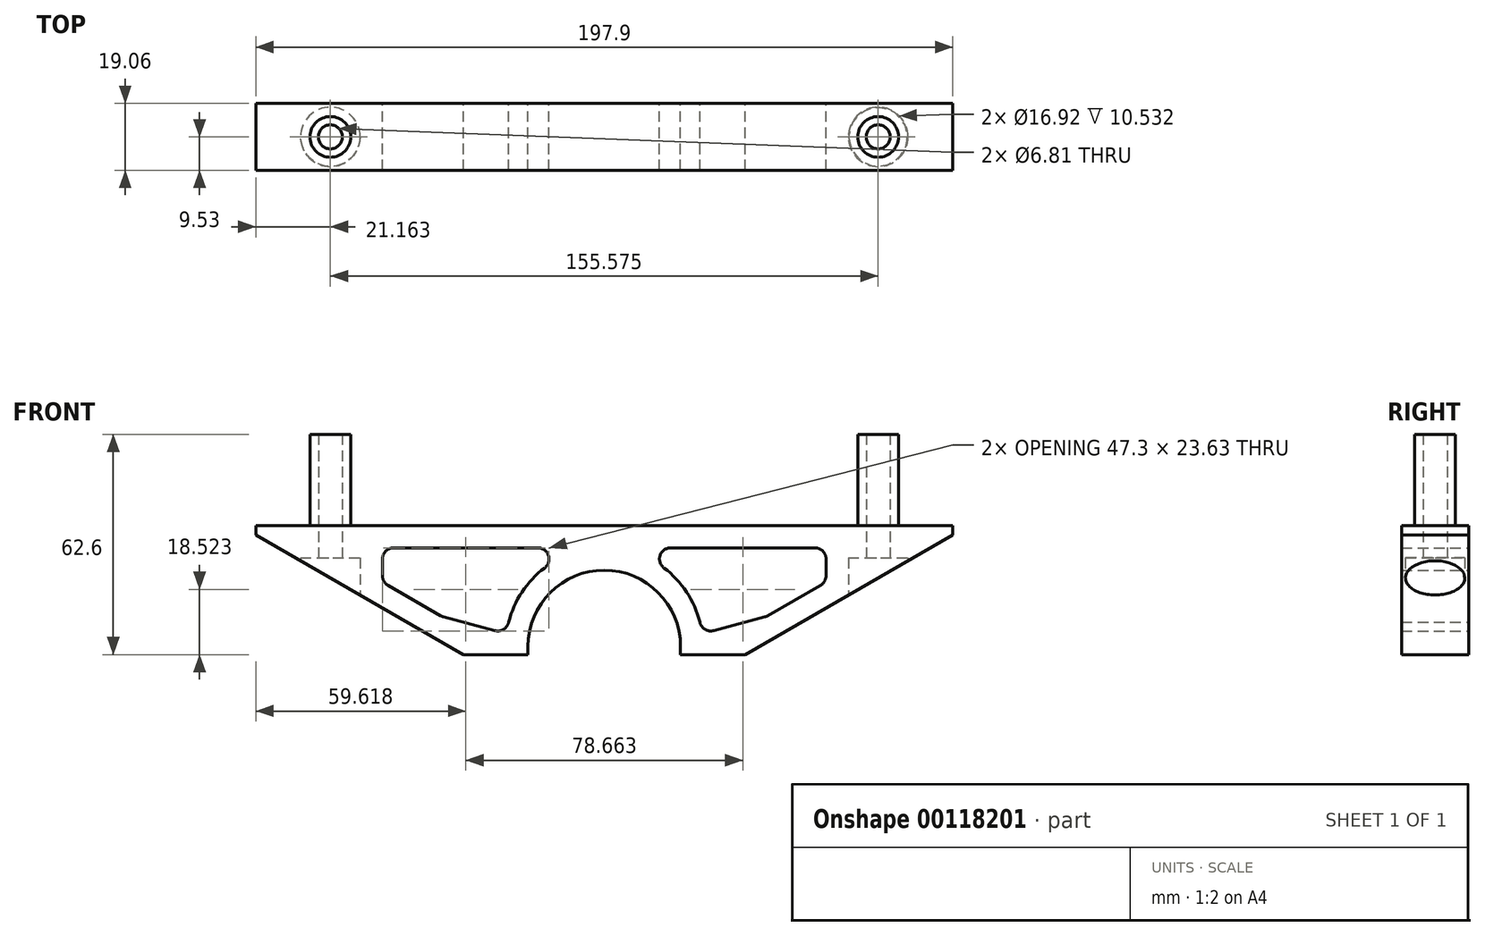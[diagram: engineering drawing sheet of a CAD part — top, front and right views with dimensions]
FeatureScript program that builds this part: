
annotation { "Feature Type Name" : "Feature", "Feature Type Description" : "" }
export const myFeature = defineFeature(function(context is Context, id is Id, definition is map)
    precondition{}
    {
        {
            var Q0;
            Q0=qCreatedBy(makeId("Front.planeOp"),FACE);
            var sketch = newSketch(context, id + "F0", { "sketchPlane" : qUnion([Q0])});
            skLineSegment(sketch, "E0", {"start": v(0, 0) * mm, "end": v(0, 74.83) * mm, "construction": true});
            skLineSegment(sketch, "E1", {"start": v(40, 0) * mm, "end": v(21.65, 0) * mm});
            skArc(sketch, "E2", {"start": v(21.65, 2.33) * mm, "mid": v(0, 23.99) * mm, "end": v(-21.65, 2.33) * mm});
            skArc(sketch, "E3", {"start": v(27.19, 9.05) * mm, "mid": v(23.4, 17.72) * mm, "end": v(16.94, 24.63) * mm});
            skLineSegment(sketch, "E4", {"start": v(-98.95, 36.69) * mm, "end": v(98.95, 36.69) * mm});
            skLineSegment(sketch, "E5", {"start": v(40, 0) * mm, "end": v(98.95, 34.03) * mm});
            skLineSegment(sketch, "E6", {"start": v(-40, 0) * mm, "end": v(-98.95, 34.03) * mm});
            skLineSegment(sketch, "E7", {"start": v(-98.95, 36.69) * mm, "end": v(-98.95, 34.03) * mm});
            skLineSegment(sketch, "E8", {"start": v(98.95, 36.69) * mm, "end": v(98.95, 34.03) * mm});
            skLineSegment(sketch, "E9", {"start": v(21.65, 2.33) * mm, "end": v(21.65, -7.41) * mm});
            skLineSegment(sketch, "E10", {"start": v(-21.65, 2.33) * mm, "end": v(-21.65, 0) * mm});
            skLineSegment(sketch, "E11.trimOffspring", {"start": v(-21.65, 0) * mm, "end": v(-40, 0) * mm});
            skArc(sketch, "E12", {"start": v(18.86, 30.34) * mm, "mid": v(15.85, 28.18) * mm, "end": v(16.94, 24.63) * mm});
            skArc(sketch, "E13", {"start": v(27.16, 9.17) * mm, "mid": v(28.61, 7.16) * mm, "end": v(31.07, 6.81) * mm});
            skArc(sketch, "E14", {"start": v(45.65, 10.72) * mm, "mid": v(46.04, 10.85) * mm, "end": v(46.42, 11.03) * mm});
            skLineSegment(sketch, "E15", {"start": v(18.86, 30.34) * mm, "end": v(59.8, 30.34) * mm});
            skLineSegment(sketch, "E16", {"start": v(62.98, 27.16) * mm, "end": v(62.98, 22.43) * mm});
            skLineSegment(sketch, "E17", {"start": v(61.4, 19.68) * mm, "end": v(46.42, 11.03) * mm});
            skLineSegment(sketch, "E18", {"start": v(45.65, 10.72) * mm, "end": v(31.07, 6.81) * mm});
            skArc(sketch, "E19.trimOffspring", {"start": v(62.98, 27.16) * mm, "mid": v(62.05, 29.4) * mm, "end": v(59.8, 30.34) * mm});
            skArc(sketch, "E20.trimOffspring", {"start": v(61.4, 19.68) * mm, "mid": v(62.55, 20.84) * mm, "end": v(62.98, 22.43) * mm});
            skArc(sketch, "E21.MirrorCS", {"start": v(-18.86, 30.34) * mm, "mid": v(-15.85, 28.18) * mm, "end": v(-16.94, 24.63) * mm});
            skLineSegment(sketch, "E22.MirrorCS", {"start": v(-18.86, 30.34) * mm, "end": v(-59.8, 30.34) * mm});
            skArc(sketch, "E23.MirrorCS", {"start": v(-27.19, 9.05) * mm, "mid": v(-23.4, 17.72) * mm, "end": v(-16.94, 24.63) * mm});
            skArc(sketch, "E24.MirrorCS", {"start": v(-27.16, 9.17) * mm, "mid": v(-28.61, 7.16) * mm, "end": v(-31.07, 6.81) * mm});
            skArc(sketch, "E25.MirrorCS", {"start": v(-45.65, 10.72) * mm, "mid": v(-46.04, 10.85) * mm, "end": v(-46.42, 11.03) * mm});
            skLineSegment(sketch, "E26.MirrorCS", {"start": v(-61.4, 19.68) * mm, "end": v(-46.42, 11.03) * mm});
            skLineSegment(sketch, "E27.MirrorCS", {"start": v(-62.98, 27.16) * mm, "end": v(-62.98, 22.43) * mm});
            skArc(sketch, "E28.MirrorCS", {"start": v(-62.98, 27.16) * mm, "mid": v(-62.05, 29.4) * mm, "end": v(-59.8, 30.34) * mm});
            skLineSegment(sketch, "E29.MirrorCS", {"start": v(-45.65, 10.72) * mm, "end": v(-31.07, 6.81) * mm});
            skArc(sketch, "E30.MirrorCS", {"start": v(-61.4, 19.68) * mm, "mid": v(-62.55, 20.84) * mm, "end": v(-62.98, 22.43) * mm});
            skSolve(sketch);
        }
        {
            var Q0;
            {var subQ8=sQuery(id+"F0.wireOp",EDGE,"E1");Q0=makeQuery(id+"F0.imprint","IMPRINT",FACE,{"disambiguationData":[TD([[makeQuery(id+"F0.imprint","IMPRINT",EDGE,{"derivedFrom":subQ8}),-1.0]])]});}
            extrude(context, id + "F1", {"entities" : qUnion([Q0]), "endBound" : BoundingType.SYMMETRIC, "depth" : 19.05 * mm});
        }
        {
            var Q0;
            Q0=makeQuery(id+"F1.opExtrude","SWEPT_FACE",FACE,{"disambiguationData":[OSD([sQuery(id+"F0.wireOp",EDGE,"E11.trimOffspring")])]});
            cPlane(context, id + "F2", {"entities" : qUnion([Q0]), "cplaneType" : CPlaneType.OFFSET, "offset" : 0 * mm, "width" : 152.4 * mm, "height" : 152.4 * mm});
        }
        {
            var Q0;
            Q0=qCreatedBy(id+"F2.planeOp",FACE);
            var sketch = newSketch(context, id + "F3", { "sketchPlane" : qUnion([Q0])});
            skCircle(sketch, "E31", {"center": v(-77.79, 0) * mm, "radius": 8.46 * mm});
            skCircle(sketch, "E32", {"center": v(77.79, 0) * mm, "radius": 8.46 * mm});
            skSolve(sketch);
        }
        {
            var Q0;
            Q0=makeQuery(id+"F3.imprint","IMPRINT",FACE,{"disambiguationData":[TD([[makeQuery(id+"F3.imprint","IMPRINT",EDGE,{"derivedFrom":sQuery(id+"F3.wireOp",EDGE,"E31")}),1.0]])]});
            var Q1;
            Q1=makeQuery(id+"F3.imprint","IMPRINT",FACE,{"disambiguationData":[TD([[makeQuery(id+"F3.imprint","IMPRINT",EDGE,{"derivedFrom":sQuery(id+"F3.wireOp",EDGE,"E32")}),1.0]])]});
            extrude(context, id + "F4", {"entities" : qUnion([Q0, Q1]), "operationType" : NewBodyOperationType.REMOVE, "oppositeDirection" : true, "depth" : 27.46 * mm});
        }
        {
            var Q0;
            Q0=makeQuery(id+"F1.opExtrude","SWEPT_FACE",FACE,{"disambiguationData":[OSD([sQuery(id+"F0.wireOp",EDGE,"E4")])]});
            cPlane(context, id + "F5", {"entities" : qUnion([Q0]), "cplaneType" : CPlaneType.OFFSET, "offset" : 0 * mm, "width" : 152.4 * mm, "height" : 152.4 * mm});
        }
        {
            var Q0;
            Q0=qCreatedBy(id+"F5.planeOp",FACE);
            var sketch = newSketch(context, id + "F6", { "sketchPlane" : qUnion([Q0])});
            skCircle(sketch, "E33", {"center": v(-77.79, 0) * mm, "radius": 5.78 * mm});
            skCircle(sketch, "E34", {"center": v(77.79, 0) * mm, "radius": 5.78 * mm});
            skSolve(sketch);
        }
        {
            var Q0;
            Q0 = qSketchRegion(id + "F6", true);
            extrude(context, id + "F7", {"entities" : qUnion([Q0]), "operationType" : NewBodyOperationType.ADD, "depth" : 25.9 * mm});
        }
        {
            var Q0;
            Q0=qCreatedBy(id+"F2.planeOp",FACE);
            var sketch = newSketch(context, id + "F8", { "sketchPlane" : qUnion([Q0])});
            skCircle(sketch, "E35", {"center": v(-77.79, 0) * mm, "radius": 3.4 * mm});
            skCircle(sketch, "E36", {"center": v(77.79, 0) * mm, "radius": 3.4 * mm});
            skSolve(sketch);
        }
        {
            var Q0;
            Q0 = qSketchRegion(id + "F8", true);
            extrude(context, id + "F9", {"entities" : qUnion([Q0]), "operationType" : NewBodyOperationType.REMOVE, "oppositeDirection" : true, "depth" : 76.2 * mm});
        }
    });
